# Revit family: Noon 303
name_source: partatom
category: Мебель
revit_build: Autodesk Revit 2017 (Build: 20160225_1515(x64)
units: mm (PartAtom-declared; Revit-internal decimal feet)

## family parameters
Всегда вертикально = Да
Заголовок OmniClass = General Furniture and Specialties
На основе рабочей плоскости = Нет
Номер OmniClass = 23.40.20.00
Общий = Нет
При загрузке вырезать с полостями = Нет
Точка расчета площади = Нет

## types (4) — shared parameters
Fabric = Skandiform Fabric
Leg = Skandiform Chrome
Изготовитель = Skandiform AB
Ключевая пометка = XBF.4
Комментарии к типоразмеру = Created by Astacus AB
Описание = Silver lacquered chassis.

## per-type parameters (varying)
| type | Type | URL | Группа модели |
| SA-302 | SA-302 | http://www.biminfo.se | SA-302 |
| SA-303 | SA-303 | http://www.biminfo.se | SA-303 |
| SA-304 | SA-304 | http://www.biminfo.se | SA-304 |
| SA-305 | SA-303 | http://file-system.ru | SA-303 |

## geometry (parser evidence)
native form markers: Blend x4, Sweep x14
no freeform markers — native parametric forms only
